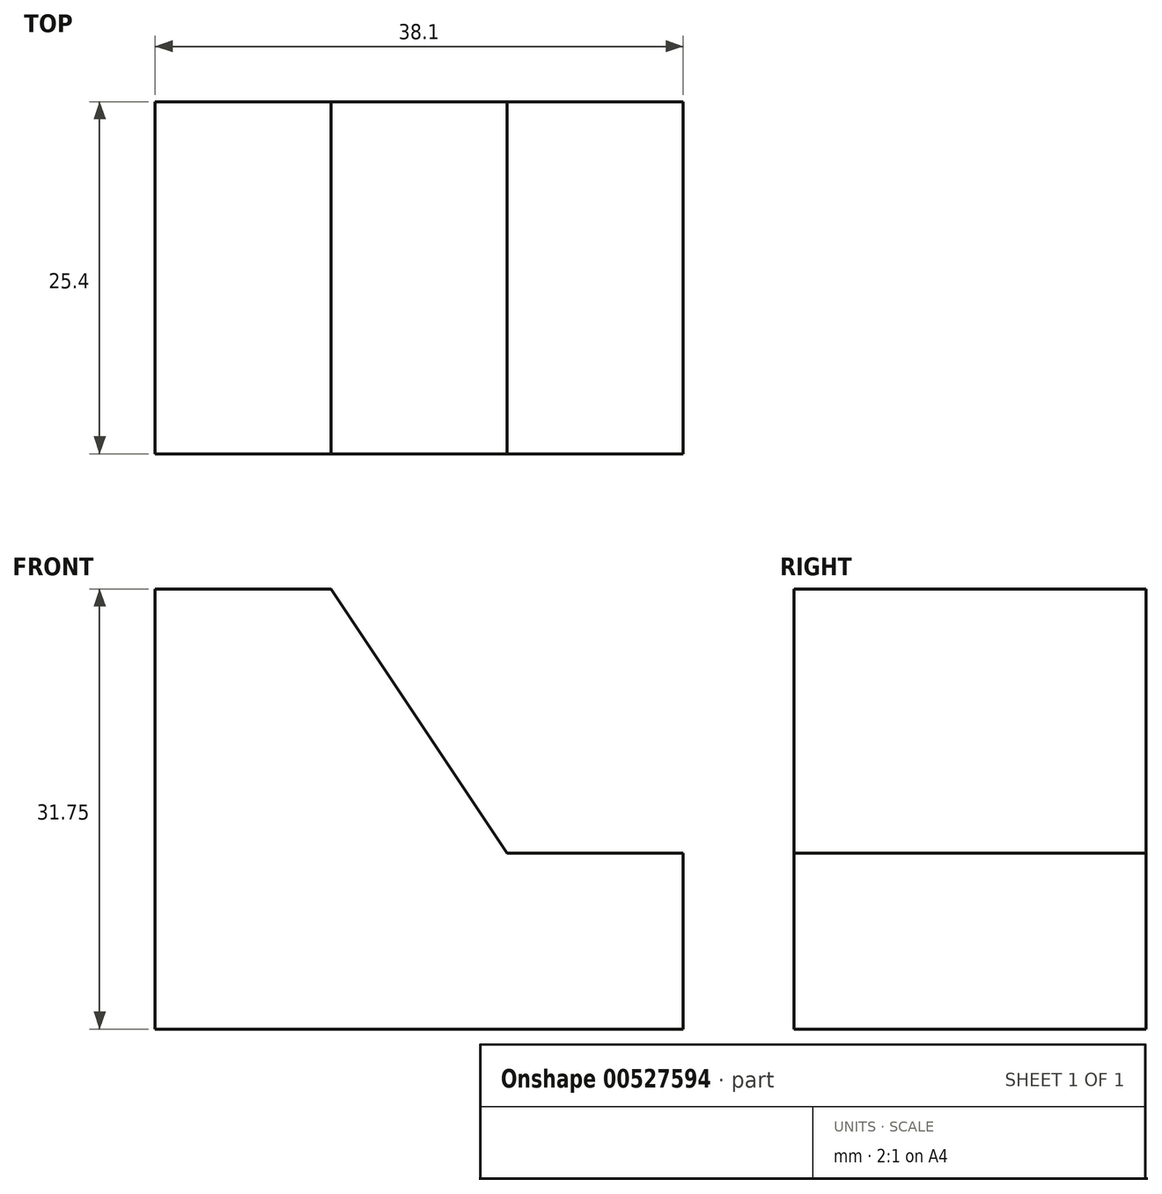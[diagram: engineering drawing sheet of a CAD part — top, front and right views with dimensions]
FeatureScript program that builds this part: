
annotation { "Feature Type Name" : "Feature", "Feature Type Description" : "" }
export const myFeature = defineFeature(function(context is Context, id is Id, definition is map)
    precondition{}
    {
        {
            var Q0;
            Q0=qCreatedBy(makeId("Front.planeOp"),FACE);
            var sketch = newSketch(context, id + "F0", { "sketchPlane" : qUnion([Q0])});
            skLineSegment(sketch, "E0", {"start": v(0, 0) * mm, "end": v(38.1, 0) * mm});
            skLineSegment(sketch, "E1", {"start": v(38.1, 0) * mm, "end": v(38.1, 31.75) * mm});
            skLineSegment(sketch, "E2", {"start": v(38.1, 31.75) * mm, "end": v(0, 31.75) * mm});
            skLineSegment(sketch, "E3", {"start": v(0, 31.75) * mm, "end": v(0, 0) * mm});
            skSolve(sketch);
        }
        {
            var Q0;
            Q0=makeQuery(id+"F0.imprint","IMPRINT",FACE,{"disambiguationData":[TD([[makeQuery(id+"F0.imprint","IMPRINT",EDGE,{"derivedFrom":sQuery(id+"F0.wireOp",EDGE,"E0")}),1.0]])]});
            extrude(context, id + "F1", {"entities" : qUnion([Q0]), "depth" : 25.4 * mm, "offsetDistance" : 25.4 * mm});
        }
        {
            var Q0;
            Q0=makeQuery(id+"F1.opExtrude","CAP_FACE",FACE,{"disambiguationData":[OSD([sQuery(id+"F0.wireOp",EDGE,"E0"),sQuery(id+"F0.wireOp",EDGE,"E1"),sQuery(id+"F0.wireOp",EDGE,"E2"),sQuery(id+"F0.wireOp",EDGE,"E3")])],"isStart":false});
            var sketch = newSketch(context, id + "F2", { "sketchPlane" : qUnion([Q0])});
            skLineSegment(sketch, "E4", {"start": v(0, 31.75) * mm, "end": v(12.7, 31.75) * mm});
            skLineSegment(sketch, "E5", {"start": v(12.7, 31.75) * mm, "end": v(25.4, 12.7) * mm});
            skLineSegment(sketch, "E6", {"start": v(25.4, 12.7) * mm, "end": v(38.1, 12.7) * mm});
            skSolve(sketch);
        }
        {
            var Q0;
            {var subQ0=sQuery(id+"F2.wireOp",EDGE,"E5");Q0=makeQuery(id+"F2.imprint","IMPRINT",FACE,{"disambiguationData":[TD([[makeQuery(id+"F2.imprint","IMPRINT",EDGE,{"derivedFrom":subQ0}),1.0]])]});}
            extrude(context, id + "F3", {"entities" : qUnion([Q0]), "operationType" : NewBodyOperationType.REMOVE, "oppositeDirection" : true, "depth" : 25.4 * mm, "offsetDistance" : 25.4 * mm});
        }
    });
